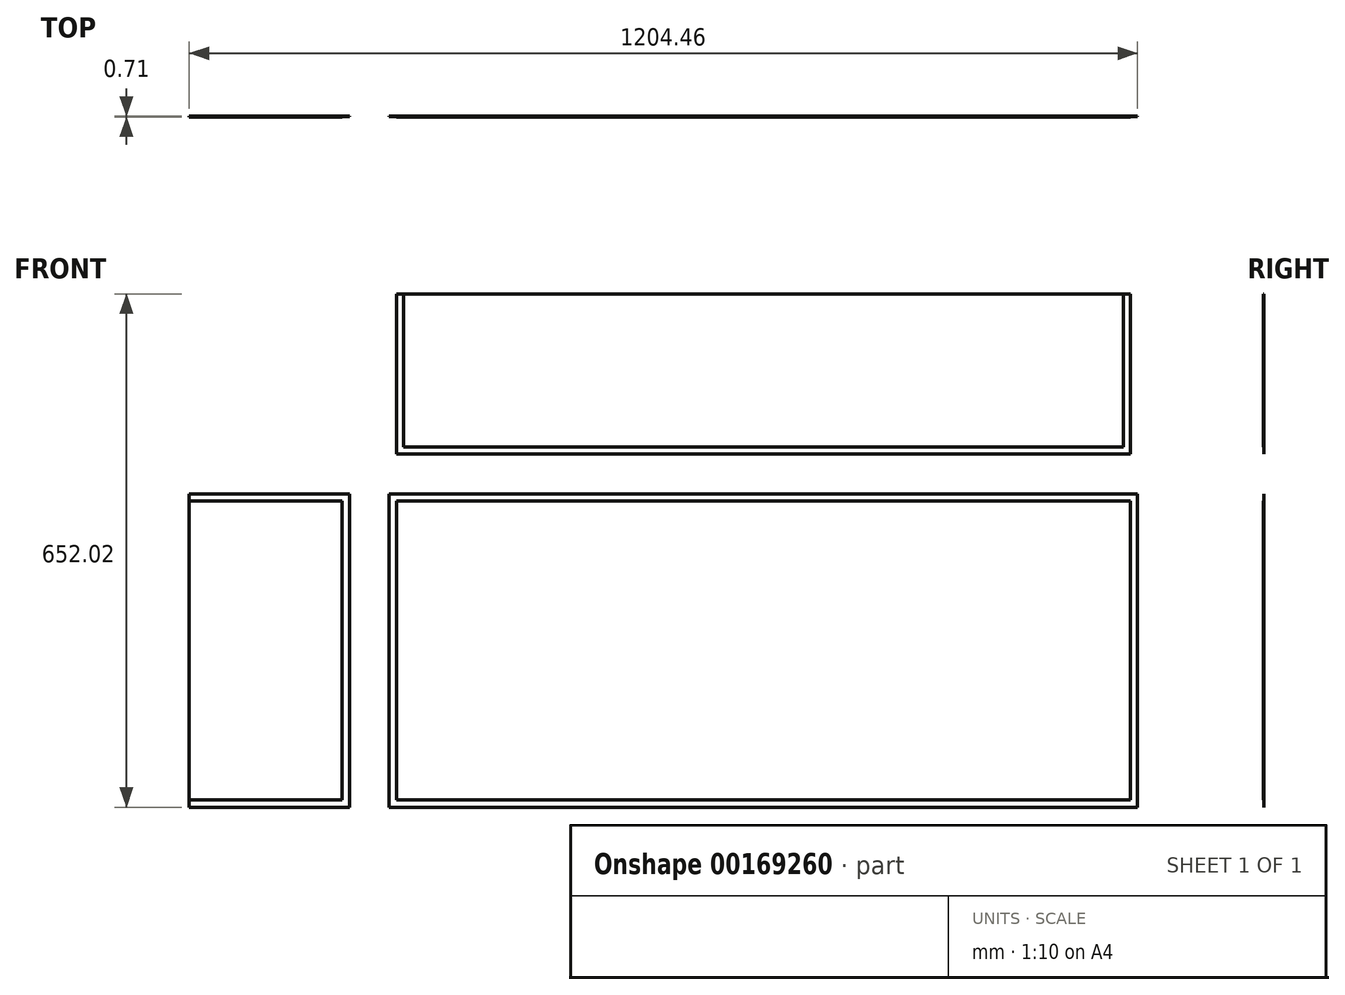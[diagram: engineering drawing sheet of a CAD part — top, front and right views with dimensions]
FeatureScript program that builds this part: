
annotation { "Feature Type Name" : "Feature", "Feature Type Description" : "" }
export const myFeature = defineFeature(function(context is Context, id is Id, definition is map)
    precondition{}
    {
        {
            assignVariable(context, id + "F0", {"name" : "ply34", "anyValue" : .71});
        }
        {
            var Q0;
            Q0=qCreatedBy(makeId("Front.planeOp"),FACE);
            var sketch = newSketch(context, id + "F1", { "sketchPlane" : qUnion([Q0])});
            skLineSegment(sketch, "E0.bottom", {"start": v(-457.2, 180.98) * mm, "end": v(457.2, 180.98) * mm, "construction": true});
            skLineSegment(sketch, "E0.top", {"start": v(-457.2, -180.98) * mm, "end": v(457.2, -180.98) * mm, "construction": true});
            skLineSegment(sketch, "E0.left", {"start": v(-457.2, 180.98) * mm, "end": v(-457.2, -180.97) * mm, "construction": true});
            skLineSegment(sketch, "E0.right", {"start": v(457.2, 180.98) * mm, "end": v(457.2, -180.97) * mm, "construction": true});
            skPoint(sketch, "E0.middle", {"position": v(0, 0) * mm});
            skLineSegment(sketch, "E1.0", {"start": v(-466.22, 190) * mm, "end": v(466.22, 190) * mm});
            skLineSegment(sketch, "E1.1", {"start": v(-466.22, 190) * mm, "end": v(-466.22, -190) * mm});
            skLineSegment(sketch, "E1.2", {"start": v(-466.22, -190) * mm, "end": v(466.22, -190) * mm});
            skLineSegment(sketch, "E1.3", {"start": v(466.22, 190) * mm, "end": v(466.22, -190) * mm});
            skLineSegment(sketch, "E2.0", {"start": v(-475.23, 199) * mm, "end": v(-475.23, -199) * mm});
            skLineSegment(sketch, "E2.1", {"start": v(-475.23, 199) * mm, "end": v(475.23, 199) * mm});
            skLineSegment(sketch, "E2.2", {"start": v(475.23, 199) * mm, "end": v(475.23, -199) * mm});
            skLineSegment(sketch, "E2.3", {"start": v(-475.23, -199) * mm, "end": v(475.23, -199) * mm});
            skLineSegment(sketch, "E3.bottom", {"start": v(-526.03, 199) * mm, "end": v(-729.23, 199) * mm});
            skLineSegment(sketch, "E3.top", {"start": v(-526.03, -199) * mm, "end": v(-729.23, -199) * mm});
            skLineSegment(sketch, "E3.left", {"start": v(-526.03, 199) * mm, "end": v(-526.03, -199) * mm});
            skLineSegment(sketch, "E3.right", {"start": v(-729.23, 199) * mm, "end": v(-729.23, -199) * mm});
            skLineSegment(sketch, "E4", {"start": v(-526.03, 190) * mm, "end": v(-729.23, 190) * mm});
            skLineSegment(sketch, "E5", {"start": v(-526.03, -190) * mm, "end": v(-729.23, -190) * mm});
            skLineSegment(sketch, "E6", {"start": v(-535.05, 190) * mm, "end": v(-535.05, -190) * mm});
            skLineSegment(sketch, "E7.bottom", {"start": v(466.22, 249.8) * mm, "end": v(-466.22, 249.8) * mm});
            skLineSegment(sketch, "E7.top", {"start": v(466.22, 453) * mm, "end": v(-466.22, 453) * mm});
            skLineSegment(sketch, "E7.left", {"start": v(466.22, 249.8) * mm, "end": v(466.22, 453) * mm});
            skLineSegment(sketch, "E7.right", {"start": v(-466.22, 249.8) * mm, "end": v(-466.22, 453) * mm});
            skLineSegment(sketch, "E8", {"start": v(-457.2, 249.8) * mm, "end": v(-457.2, 453) * mm});
            skLineSegment(sketch, "E9", {"start": v(457.2, 249.8) * mm, "end": v(457.2, 453) * mm});
            skLineSegment(sketch, "E10", {"start": v(-457.2, 258.83) * mm, "end": v(457.2, 258.83) * mm});
            skSolve(sketch);
        }
        {
            var Q0;
            {var subQ5=sQuery(id+"F1.wireOp",EDGE,"E10");Q0=makeQuery(id+"F1.imprint","IMPRINT",FACE,{"disambiguationData":[TD([[makeQuery(id+"F1.imprint","IMPRINT",EDGE,{"derivedFrom":subQ5}),1.0]])]});}
            var Q1;
            Q1=makeQuery(id+"F1.imprint","IMPRINT",FACE,{"disambiguationData":[TD([[makeQuery(id+"F1.imprint","IMPRINT",EDGE,{"derivedFrom":sQuery(id+"F1.wireOp",EDGE,"E1.0")}),-1.0]])]});
            var Q2;
            {var subQ5=sQuery(id+"F1.wireOp",EDGE,"E6");Q2=makeQuery(id+"F1.imprint","IMPRINT",FACE,{"disambiguationData":[TD([[makeQuery(id+"F1.imprint","IMPRINT",EDGE,{"derivedFrom":subQ5}),-1.0]])]});}
            extrude(context, id + "F2", {"entities" : qUnion([Q0, Q1, Q2]), "depth" : (getVariable(context, 'ply34')) * mm});
        }
        {
            var Q0;
            {var subQ0=sQuery(id+"F1.wireOp",EDGE,"E7.right");Q0=makeQuery(id+"F1.imprint","IMPRINT",FACE,{"disambiguationData":[TD([[makeQuery(id+"F1.imprint","IMPRINT",EDGE,{"derivedFrom":subQ0}),-1.0]])]});}
            var Q1;
            Q1=makeQuery(id+"F1.imprint","IMPRINT",FACE,{"disambiguationData":[TD([[makeQuery(id+"F1.imprint","IMPRINT",EDGE,{"derivedFrom":sQuery(id+"F1.wireOp",EDGE,"E1.0")}),1.0]])]});
            var Q2;
            {var subQ5=sQuery(id+"F1.wireOp",EDGE,"E3.bottom");Q2=makeQuery(id+"F1.imprint","IMPRINT",FACE,{"disambiguationData":[TD([[makeQuery(id+"F1.imprint","IMPRINT",EDGE,{"derivedFrom":subQ5}),1.0]])]});}
            var Q3;
            {var subQ5=sQuery(id+"F1.wireOp",EDGE,"E6");Q3=makeQuery(id+"F1.imprint","IMPRINT",FACE,{"disambiguationData":[TD([[makeQuery(id+"F1.imprint","IMPRINT",EDGE,{"derivedFrom":subQ5}),1.0]])]});}
            var Q4;
            {var subQ5=sQuery(id+"F1.wireOp",EDGE,"E3.top");Q4=makeQuery(id+"F1.imprint","IMPRINT",FACE,{"disambiguationData":[TD([[makeQuery(id+"F1.imprint","IMPRINT",EDGE,{"derivedFrom":subQ5}),-1.0]])]});}
            var Q5;
            {var subQ0=sQuery(id+"F1.wireOp",EDGE,"E7.left");Q5=makeQuery(id+"F1.imprint","IMPRINT",FACE,{"disambiguationData":[TD([[makeQuery(id+"F1.imprint","IMPRINT",EDGE,{"derivedFrom":subQ0}),1.0]])]});}
            var Q6;
            {var subQ5=sQuery(id+"F1.wireOp",EDGE,"E10");Q6=makeQuery(id+"F1.imprint","IMPRINT",FACE,{"disambiguationData":[TD([[makeQuery(id+"F1.imprint","IMPRINT",EDGE,{"derivedFrom":subQ5}),-1.0]])]});}
            extrude(context, id + "F3", {"entities" : qUnion([Q0, Q1, Q2, Q3, Q4, Q5, Q6]), "operationType" : NewBodyOperationType.ADD, "depth" : (getVariable(context, 'ply34') / 2) * mm});
        }
    });
